# Revit family: SC 1401 SMD
name_source: partatom
category: Lighting Fixtures
revit_build: Autodesk Revit 2017 (Build: 20160225_1515(x64)
units: mm (PartAtom-declared; Revit-internal decimal feet)

## family parameters
Cut with Voids When Loaded = No
Host = Face
Light Source = Yes
Part Type = Normal
Room Calculation Point = No
Round Connector Dimension = Use Diameter
Shared = No

## types (6) — shared parameters
Color Filter = 16777215
Default Elevation = 1219 mm
Description = PENDANT - MICRO LENS (DIRECT)
Dimming Lamp Color Temperature Shift = <None>
Emit Shape Visible in Rendering = Yes
Emit from Rectangle Length = 49 mm  [stored 0.160761 ft]
Emit from Rectangle Width = 1401 mm
Lamp = LED
Manufacturer = ARLIGHT
Model = SC1401SMD
Tilt Angle = 90.00°
Type Comments = STELLA-CONT-END

## per-type parameters (varying)
| type | Apparent Load | Photometric Web File | Type Image | Wattage Comments |
| SCSMD.1401.64.40 | 64 VA | SC 1401 SMD-64W-4K(SG-350mA).IES | stella_black_pendant.png | 64 |
| SCSMD.1401.64.30 | 64 VA | SC 1401 SMD-64W-3K(SG-350mA).IES | <None> | 64 |
| SCSMD.1401.38.40 | 38 VA | SC 1401 SMD-38W-4K(SG-200mA).IES | <None> | 38 |
| SCSMD.1401.38.30 | 38 VA | SC 1401 SMD-38W-3K(SG-200mA).IES | <None> | 38 |
| SCSMD.1401.22.30 | 22 VA | SC 1401 SMD-22W-3K(SG-120mA).IES | <None> | 22 |
| SCSMD.1401.22.40 | 22 VA | SC 1401 SMD-22W-4K(SG-120mA).IES | <None> | 22 |

note: [stored X ft] marks values corroborated as IEEE doubles in the binary element streams (Revit-internal decimal feet)

## geometry (parser evidence)
native form markers: Sweep x1
no freeform markers — native parametric forms only
